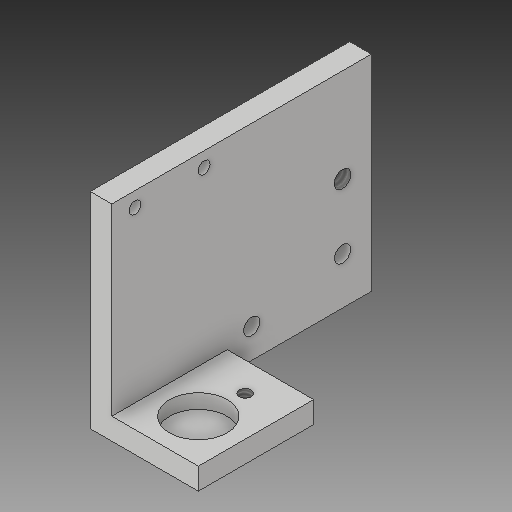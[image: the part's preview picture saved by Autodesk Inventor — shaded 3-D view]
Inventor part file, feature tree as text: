
AUTODESK INVENTOR PART (.ipt)
format: ipt  version: 2019 (Build 230136000, 136)  size: 176,640 bytes
history: native  units: in
note: dims shown in document units (in); Inventor stores cm internally (conversion verified against a paired STEP export)
features: sketch x8, projected_geometry x7, hole x6, extrude x3
ambient origin geometry x8: Origin, YZ Plane, XZ Plane, XY Plane, X Axis, Y Axis, Z Axis, Center Point
bodies: Solid1 (feature_tree)
feature tree (24):
  extrude  "Extrusion1"  Depth=2.25in
  extrude  "Extrusion3"  Depth=0.1875in
  extrude  "Extrusion4"  Depth=0.3125in TaperAngle=0.0deg
  hole  "Hole1"  [1 undecoded]
  hole  "Hole2"  [1 undecoded]
  hole  "Hole3"  [1 undecoded]
  hole  "Hole4"  [1 undecoded]
  hole  "Hole5"  [1 undecoded]
  hole  "Hole6"  [1 undecoded]
  sketch  "Sketch1"  dims[d0=1.7812in d1=2.25in]
  sketch  "Sketch3"  dims[d2=0.1875in d3=0.0in d8=0.1875in]
  projected_geometry  "Projected Loop2"
  projected_geometry  "Projected Loop3"
  sketch  "Sketch5"  dims[d9=0.75in d10=0.0in d13=0.3125in d14=0.0in]
  projected_geometry  "Projected Loop4"
  sketch  "Sketch6"  dims[d15=0.1875in d16=0.8125in d17=0.25in]
  projected_geometry  "Projected Loop6"
  sketch  "Sketch10"  dims[d18=0.145in d19=0.38in d20=0.375in d21=0.25in d22=0.5635in d23=0.588in d24=0.8108in d25=0.375in]
  projected_geometry  "Projected Loop10"
  sketch  "Sketch11"  dims[d26=0.375in]
  projected_geometry  "Projected Loop11"
  sketch  "Sketch12"  dims[d27=0.5in d28=0.75in d29=0.375in d30=0.25in d31=0.5635in d32=0.125in d33=0.0in d48=0.625in]
  projected_geometry  "Projected Loop12"
  sketch  "Sketch13"  dims[d49=0.5in d50=0.5in d51=0.104in d52=0.276in d53=0.375in d54=0.25in d55=0.5635in d56=0.432in d57=0.8108in d58=0.25in d59=0.104in d60=0.276in d61=0.375in d62=0.25in d63=0.5635in d64=0.432in d65=0.8108in d66=0.25in d67=0.406in d68=0.256in d69=1.0375in d70=0.14in d71=0.75in d72=0.375in d73=0.25in d74=0.5635in d75=1.0in d76=0.8108in d77=0.2in d78=0.6in d79=0.104in d80=0.75in d81=0.375in d82=0.25in d83=0.5635in d84=1.0in d85=0.8108in]
note: 6 required parameter values undecoded (feature->parameter linkage not recoverable at this tier; creation-order binding heuristic only, values carry confidence <= 0.55)
